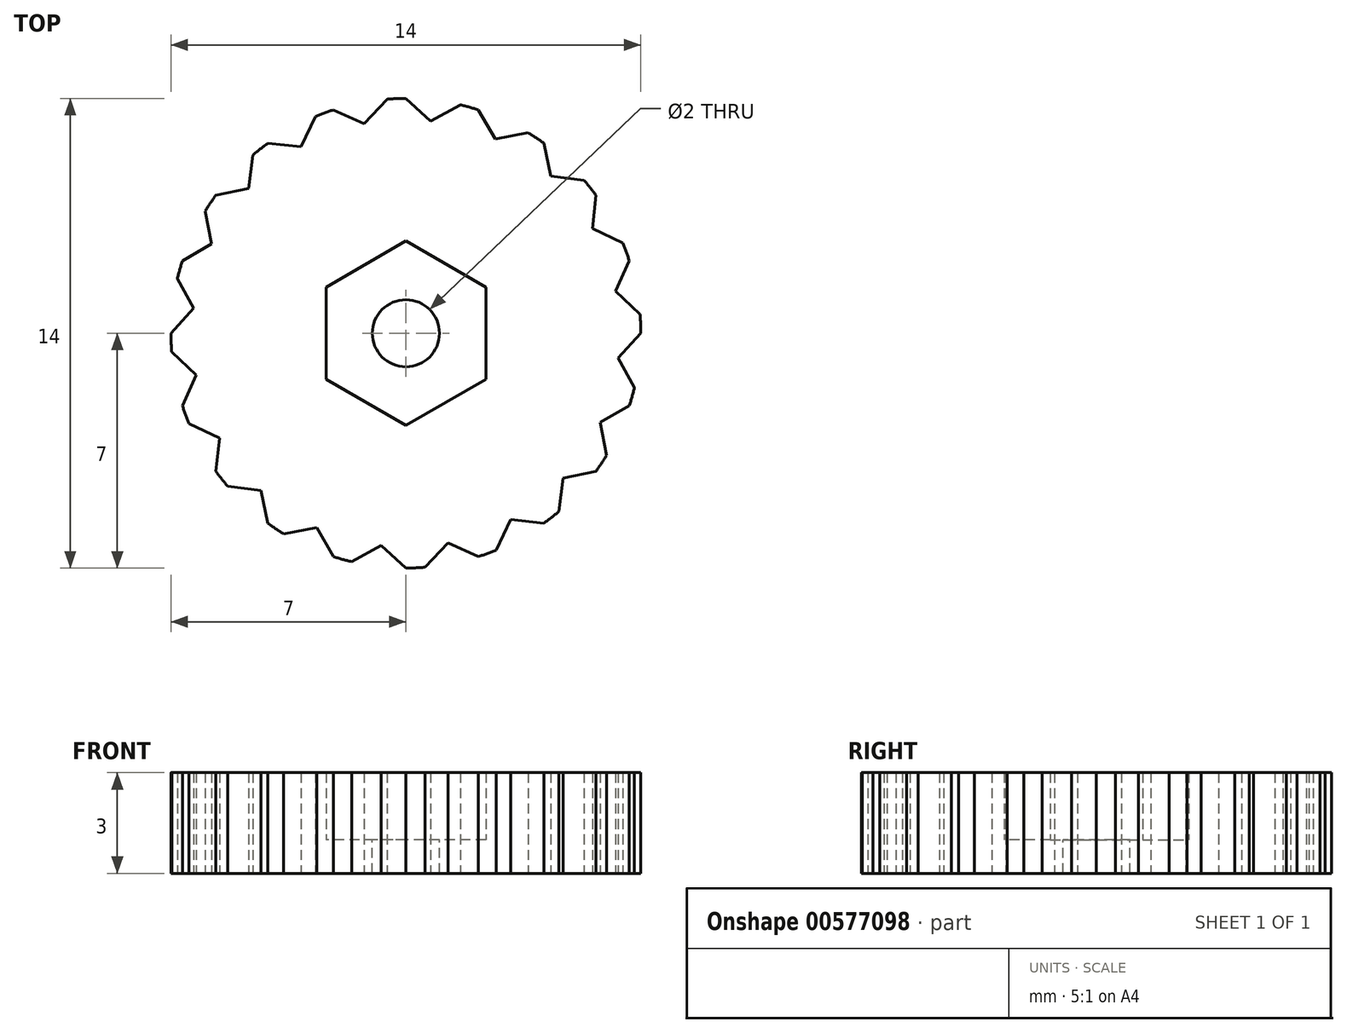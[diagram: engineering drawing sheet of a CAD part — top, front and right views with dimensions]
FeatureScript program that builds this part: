
annotation { "Feature Type Name" : "Feature", "Feature Type Description" : "" }
export const myFeature = defineFeature(function(context is Context, id is Id, definition is map)
    precondition{}
    {
        {
            var Q0;
            Q0=qCreatedBy(makeId("Top.planeOp"),FACE);
            var sketch = newSketch(context, id + "F0", { "sketchPlane" : qUnion([Q0])});
            skCircle(sketch, "E0.cCircle", {"center": v(0, 0) * mm, "radius": 2.75 * mm, "construction": true});
            skLineSegment(sketch, "E0.0", {"start": v(0, -2.75) * mm, "end": v(-2.38, -1.38) * mm});
            skLineSegment(sketch, "E0.1", {"start": v(-2.38, -1.37) * mm, "end": v(-2.38, 1.37) * mm});
            skLineSegment(sketch, "E0.2", {"start": v(-2.38, 1.37) * mm, "end": v(0, 2.75) * mm});
            skLineSegment(sketch, "E0.3", {"start": v(0, 2.75) * mm, "end": v(2.38, 1.38) * mm});
            skLineSegment(sketch, "E0.4", {"start": v(2.38, 1.38) * mm, "end": v(2.38, -1.37) * mm});
            skLineSegment(sketch, "E0.5", {"start": v(2.38, -1.37) * mm, "end": v(0, -2.75) * mm});
            skCircle(sketch, "E1", {"center": v(0, 0) * mm, "radius": 1 * mm});
            skCircle(sketch, "E2", {"center": v(0, 0) * mm, "radius": 7 * mm});
            skLineSegment(sketch, "E3", {"start": v(0, 7) * mm, "end": v(0.74, 6.33) * mm});
            skLineSegment(sketch, "E4", {"start": v(0.74, 6.33) * mm, "end": v(1.62, 6.81) * mm});
            skLineSegment(sketch, "E5.1.0", {"start": v(-2.16, 6.66) * mm, "end": v(-1.25, 6.25) * mm});
            skLineSegment(sketch, "E5.1.1", {"start": v(-1.25, 6.25) * mm, "end": v(-0.57, 6.98) * mm});
            skLineSegment(sketch, "E5.2.0", {"start": v(-4.11, 5.66) * mm, "end": v(-3.12, 5.56) * mm});
            skLineSegment(sketch, "E5.2.1", {"start": v(-3.12, 5.56) * mm, "end": v(-2.7, 6.46) * mm});
            skLineSegment(sketch, "E5.3.0", {"start": v(-5.66, 4.11) * mm, "end": v(-4.68, 4.32) * mm});
            skLineSegment(sketch, "E5.3.1", {"start": v(-4.68, 4.32) * mm, "end": v(-4.56, 5.31) * mm});
            skLineSegment(sketch, "E5.4.0", {"start": v(-6.66, 2.16) * mm, "end": v(-5.8, 2.66) * mm});
            skLineSegment(sketch, "E5.4.1", {"start": v(-5.8, 2.66) * mm, "end": v(-5.98, 3.64) * mm});
            skLineSegment(sketch, "E5.5.0", {"start": v(-7, 0) * mm, "end": v(-6.33, 0.74) * mm});
            skLineSegment(sketch, "E5.5.1", {"start": v(-6.33, 0.74) * mm, "end": v(-6.81, 1.62) * mm});
            skLineSegment(sketch, "E5.6.0", {"start": v(-6.66, -2.16) * mm, "end": v(-6.25, -1.25) * mm});
            skLineSegment(sketch, "E5.6.1", {"start": v(-6.25, -1.25) * mm, "end": v(-6.98, -0.57) * mm});
            skLineSegment(sketch, "E5.7.0", {"start": v(-5.66, -4.11) * mm, "end": v(-5.56, -3.12) * mm});
            skLineSegment(sketch, "E5.7.1", {"start": v(-5.56, -3.12) * mm, "end": v(-6.46, -2.7) * mm});
            skLineSegment(sketch, "E5.8.0", {"start": v(-4.11, -5.66) * mm, "end": v(-4.32, -4.68) * mm});
            skLineSegment(sketch, "E5.8.1", {"start": v(-4.32, -4.68) * mm, "end": v(-5.31, -4.56) * mm});
            skLineSegment(sketch, "E5.9.0", {"start": v(-2.16, -6.66) * mm, "end": v(-2.66, -5.8) * mm});
            skLineSegment(sketch, "E5.9.1", {"start": v(-2.66, -5.8) * mm, "end": v(-3.64, -5.98) * mm});
            skLineSegment(sketch, "E5.10.0", {"start": v(0, -7) * mm, "end": v(-0.74, -6.33) * mm});
            skLineSegment(sketch, "E5.10.1", {"start": v(-0.74, -6.33) * mm, "end": v(-1.62, -6.81) * mm});
            skLineSegment(sketch, "E5.11.0", {"start": v(2.16, -6.66) * mm, "end": v(1.25, -6.25) * mm});
            skLineSegment(sketch, "E5.11.1", {"start": v(1.25, -6.25) * mm, "end": v(0.57, -6.98) * mm});
            skLineSegment(sketch, "E5.12.0", {"start": v(4.11, -5.66) * mm, "end": v(3.12, -5.56) * mm});
            skLineSegment(sketch, "E5.12.1", {"start": v(3.12, -5.56) * mm, "end": v(2.7, -6.46) * mm});
            skLineSegment(sketch, "E5.13.0", {"start": v(5.66, -4.11) * mm, "end": v(4.68, -4.32) * mm});
            skLineSegment(sketch, "E5.13.1", {"start": v(4.68, -4.32) * mm, "end": v(4.56, -5.31) * mm});
            skLineSegment(sketch, "E5.14.0", {"start": v(6.66, -2.16) * mm, "end": v(5.8, -2.66) * mm});
            skLineSegment(sketch, "E5.14.1", {"start": v(5.8, -2.66) * mm, "end": v(5.98, -3.64) * mm});
            skLineSegment(sketch, "E5.15.0", {"start": v(7, 0) * mm, "end": v(6.33, -0.74) * mm});
            skLineSegment(sketch, "E5.15.1", {"start": v(6.33, -0.74) * mm, "end": v(6.81, -1.62) * mm});
            skLineSegment(sketch, "E5.16.0", {"start": v(6.66, 2.16) * mm, "end": v(6.25, 1.25) * mm});
            skLineSegment(sketch, "E5.16.1", {"start": v(6.25, 1.25) * mm, "end": v(6.98, 0.57) * mm});
            skLineSegment(sketch, "E5.17.0", {"start": v(5.66, 4.11) * mm, "end": v(5.56, 3.12) * mm});
            skLineSegment(sketch, "E5.17.1", {"start": v(5.56, 3.12) * mm, "end": v(6.46, 2.7) * mm});
            skLineSegment(sketch, "E5.18.0", {"start": v(4.11, 5.66) * mm, "end": v(4.32, 4.68) * mm});
            skLineSegment(sketch, "E5.18.1", {"start": v(4.32, 4.68) * mm, "end": v(5.31, 4.56) * mm});
            skLineSegment(sketch, "E5.19.0", {"start": v(2.16, 6.66) * mm, "end": v(2.66, 5.8) * mm});
            skLineSegment(sketch, "E5.19.1", {"start": v(2.66, 5.8) * mm, "end": v(3.64, 5.98) * mm});
            skSolve(sketch);
        }
        {
            var Q0;
            Q0=makeQuery(id+"F0.imprint","IMPRINT",FACE,{"disambiguationData":[TD([[makeQuery(id+"F0.imprint","IMPRINT",EDGE,{"derivedFrom":sQuery(id+"F0.wireOp",EDGE,"E0.0")}),1.0]])]});
            extrude(context, id + "F1", {"entities" : qUnion([Q0]), "depth" : 2 * mm, "offsetDistance" : 25 * mm});
        }
        {
            var Q0;
            Q0=makeQuery(id+"F0.imprint","IMPRINT",FACE,{"disambiguationData":[TD([[makeQuery(id+"F0.imprint","IMPRINT",EDGE,{"derivedFrom":sQuery(id+"F0.wireOp",EDGE,"E0.0")}),1.0]])]});
            var Q1;
            Q1=makeQuery(id+"F0.imprint","IMPRINT",FACE,{"disambiguationData":[TD([[makeQuery(id+"F0.imprint","IMPRINT",EDGE,{"derivedFrom":sQuery(id+"F0.wireOp",EDGE,"E0.0")}),-1.0]])]});
            extrude(context, id + "F2", {"entities" : qUnion([Q0, Q1]), "operationType" : NewBodyOperationType.ADD, "depth" : -1 * mm, "offsetDistance" : 25 * mm});
        }
    });
